# Revit family: Indirect-Water-Heater_AO_Smith-IT-600_B_B
name_source: partatom
category: Mechanical Equipment
revit_build: Autodesk Revit 2016 (Build: 20170117_1200(x64)
units: mm (PartAtom-declared; Revit-internal decimal feet)

## family parameters
Always vertical = Yes
Cut with Voids When Loaded = No
OmniClass Number = 23.75.00.00
OmniClass Title = Climate Control (HVAC)
Part Type = Normal
Room Calculation Point = No
Round Connector Dimension = Use Radius
Shared = No
Work Plane-Based = No

## types (1)
- Indirect-Water-Heater_AO_Smith-IT-600_B_B
    1er Entretien (check-up) = 3 mois après l'installation
    2ème Entretien (Entretien Général) = 12 mois après l'installation
    Assembly Code = D3010
    BIM Content Developer = CAD & Company
    BIM Content Developer URL = http://www.cadcompany.nl
    Capacité - Cuve = 643 m³
    Capacité - Échangeur Inférieur = 29.3 m³
    Charge Maximale au Sol = 884.00 kg
    Description = Cuve Indirects Fournis d’un Échangeur
    Destination / Pays = Belgique
    Diamètre (avec Isolation) = 910 mm  [stored 2.98556 ft]
    Diamètre (sans Isolation) = 750 mm  [stored 2.46063 ft]
    Débit de vidage en Continu à ΔT = 28°C = 3194
    Débit de vidage en Continu à ΔT = 44°C = 2033
    Débit de vidage en Continu à ΔT = 50°C = 1789
    Débit de vidage en Continu à ΔT = 55°C = 1626
    Débit de vidage en Continu à ΔT = 70°C = 1278
    Débit de vidage à ΔT = 28°C après 120 min. = 7515.0 L
    Débit de vidage à ΔT = 28°C après 30 min. = 2723.0 L
    Débit de vidage à ΔT = 28°C après 60 min. = 4321.0 L
    Débit de vidage à ΔT = 28°C après 90 min. = 5918.0 L
    Débit de vidage à ΔT = 44°C après 120 min. = 4782.0 L
    Débit de vidage à ΔT = 44°C après 30 min. = 1733.0 L
    Débit de vidage à ΔT = 44°C après 60 min. = 2749.0 L
    Débit de vidage à ΔT = 44°C après 90 min. = 3766.0 L
    Débit de vidage à ΔT = 50°C après 120 min. = 4208.0 L
    Débit de vidage à ΔT = 50°C après 30 min. = 1525.0 L
    Débit de vidage à ΔT = 50°C après 60 min. = 2420.0 L
    Débit de vidage à ΔT = 50°C après 90 min. = 3314.0 L
    Débit de vidage à ΔT = 55°C après 120 min. = 3826.0 L
    Débit de vidage à ΔT = 55°C après 30 min. = 1386.0 L
    Débit de vidage à ΔT = 55°C après 60 min. = 2200.0 L
    Débit de vidage à ΔT = 55°C après 90 min. = 3013.0 L
    Débit de vidage à ΔT = 70°C après 120 min. = 3006.0 L
    Débit de vidage à ΔT = 70°C après 30 min. = 1089.0 L
    Débit de vidage à ΔT = 70°C après 60 min. = 1728.0 L
    Débit de vidage à ΔT = 70°C après 90 min. = 2367.0 L
    Débit à 80ºC/60ºC - Échangeur Inférieur = 4472
    Epaisseur d'Isolation = 80 mm  [stored 0.262467 ft]
    Fabricant No. = E 7110
    Garantie Pièces = 12 mois
    Garantie sur la Cuve = 36 mois
    Guide de Produit = https://www.aosmithinternational.com
    Hauteur (avec Isolation) = 1840 mm  [stored 6.03675 ft]
    Hauteur (sans Isolation) = 1805 mm  [stored 5.92192 ft]
    Hauteur d'Emballage = 1930 mm  [stored 6.33202 ft]
    Hauteur de l'Alimentation en eau Froide = 85 mm  [stored 0.278871 ft]
    Hauteur de la Sortie d'eau Chaude = 1805 mm  [stored 5.92192 ft]
    Largeur d'Emballage = 870 mm  [stored 2.85433 ft]
    Manufacturer = A.O. Smith Water Products Company b.v.
    Max. Température de l'eau - Réservoir = 95 °C
    Model = IT 600 B B
    Nombre de modèle du produit (EAN) = 8717449250713
    Perte de Pression à 80ºC/60ºC - Échangeur Inférieur = 10400.0 Pa
    Pertes en Veille = 0 W
    Pertes en Veille - tous les jours (24h) = 0
    Poids de Transport = 251.00 kg
    Poids à vide = 241.00 kg
    Pression de Service Maximale - Réservoir = 1000000.0 Pa
    Pression de Service Maximale - Échangeur Inférieur = 1600000.0 Pa
    Production Nominale - Échangeur Inférieur = 104000 W
    Profondeur d'Emballage = 870 mm  [stored 2.85433 ft]
    Raccord d'Alimentation en Eau Froide = 2 1/2"
    Raccord de Sortie d'Eau Chaude = 2 1/2"
    Raccord de la Soupape de Vidange = 1"
    Spécifications du Produit = https://www.aosmithinternational.com
    Surface d'Échange de Chaleur - Échangeur Inférieur = 3.45 m²
    Temps de réchauffement à ΔT = 28°C = 12
    Temps de réchauffement à ΔT = 44°C = 19
    Temps de réchauffement à ΔT = 50°C = 22
    Temps de réchauffement à ΔT = 55°C = 24
    Temps de réchauffement à ΔT = 70°C = 30
    Température Maximale - Échangeur Inférieur = 110 °C
    Type d'Emballage = Plastique et Bois
    URL = https://www.aosmithinternational.com
    Workspace Diameter = 1910 mm  [stored 6.2664 ft]
    Workspace Height = 2840 mm  [stored 9.31759 ft]
    espace de travail = 955 mm  [stored 3.1332 ft]
    l'Intervalle d'Entretien = 12 mois

note: [stored X ft] marks values corroborated as IEEE doubles in the binary element streams (Revit-internal decimal feet)

## geometry (parser evidence)
native form markers: Blend x2, Sweep x22
no freeform markers — native parametric forms only
